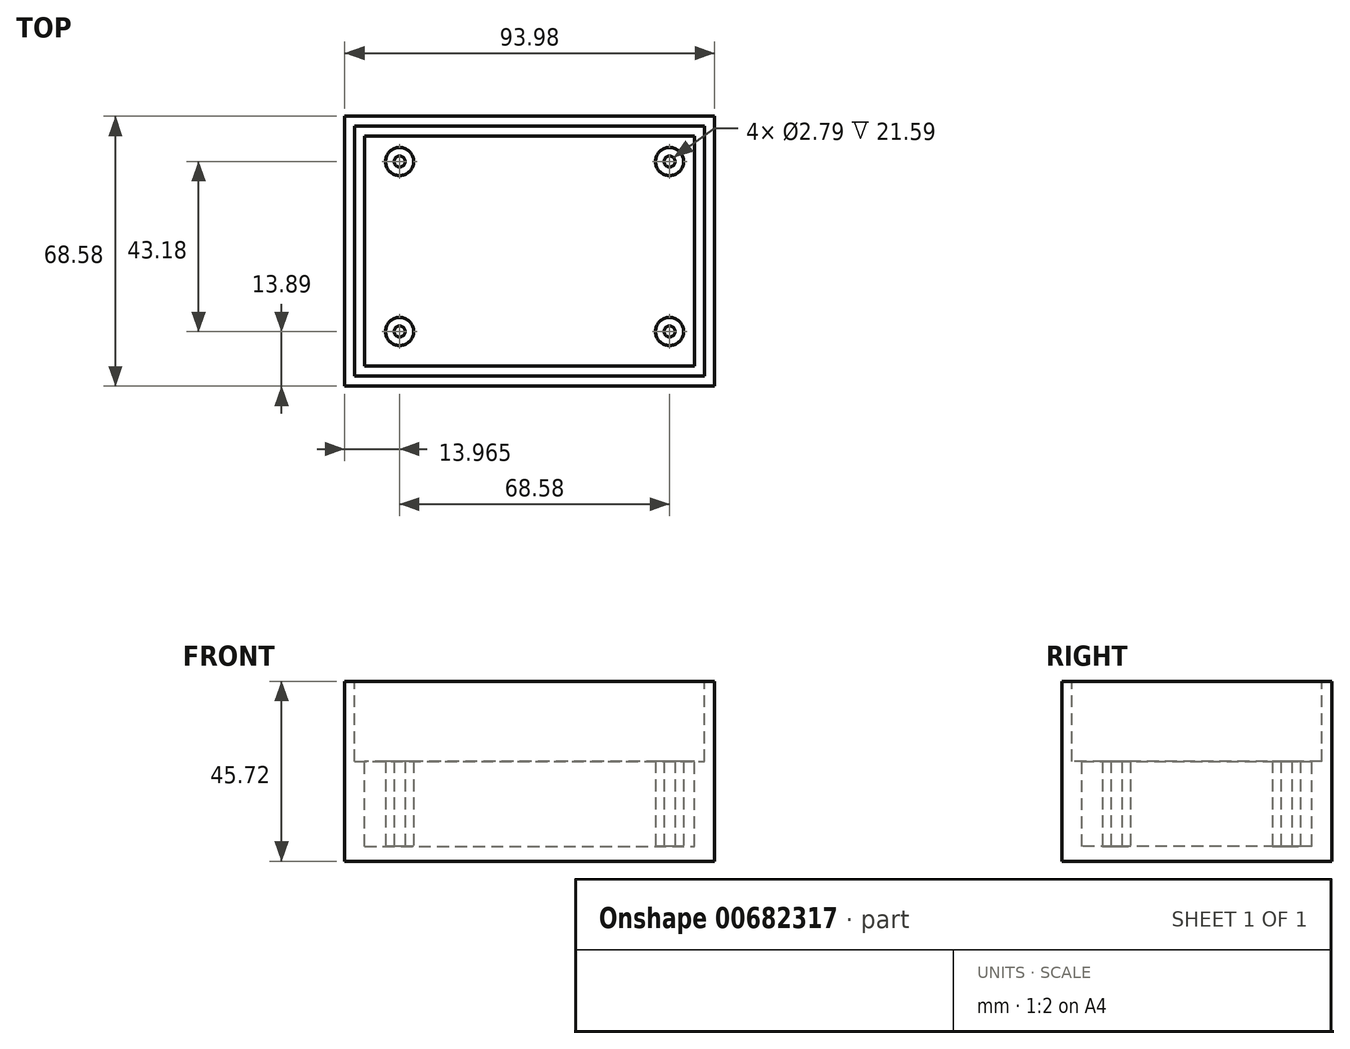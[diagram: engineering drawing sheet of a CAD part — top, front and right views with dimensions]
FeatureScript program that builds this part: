
annotation { "Feature Type Name" : "Feature", "Feature Type Description" : "" }
export const myFeature = defineFeature(function(context is Context, id is Id, definition is map)
    precondition{}
    {
        {
            var Q0;
            Q0=qCreatedBy(makeId("Top.planeOp"),FACE);
            var sketch = newSketch(context, id + "F0", { "sketchPlane" : qUnion([Q0])});
            skLineSegment(sketch, "E0.bottom", {"start": v(-123.06, 54.69) * mm, "end": v(-29.08, 54.69) * mm});
            skLineSegment(sketch, "E0.top", {"start": v(-123.06, -13.9) * mm, "end": v(-29.08, -13.9) * mm});
            skLineSegment(sketch, "E0.left", {"start": v(-123.06, 54.69) * mm, "end": v(-123.06, -13.9) * mm});
            skLineSegment(sketch, "E0.right", {"start": v(-29.08, 54.69) * mm, "end": v(-29.08, -13.9) * mm});
            skSolve(sketch);
        }
        {
            var Q0;
            Q0=makeQuery(id+"F0.imprint","IMPRINT",FACE,{"disambiguationData":[TD([[makeQuery(id+"F0.imprint","IMPRINT",EDGE,{"derivedFrom":sQuery(id+"F0.wireOp",EDGE,"E0.bottom")}),-1.0]])]});
            extrude(context, id + "F1", {"entities" : qUnion([Q0]), "depth" : 45.72 * mm, "offsetDistance" : 25.4 * mm});
        }
        {
            var Q0;
            Q0=makeQuery(id+"F1.opExtrude","CAP_FACE",FACE,{"disambiguationData":[OSD([sQuery(id+"F0.wireOp",EDGE,"E0.bottom"),sQuery(id+"F0.wireOp",EDGE,"E0.top"),sQuery(id+"F0.wireOp",EDGE,"E0.left"),sQuery(id+"F0.wireOp",EDGE,"E0.right")])],"isStart":false});
            var sketch = newSketch(context, id + "F2", { "sketchPlane" : qUnion([Q0])});
            skLineSegment(sketch, "E1.bottom", {"start": v(-117.98, 49.6) * mm, "end": v(-34.16, 49.6) * mm});
            skLineSegment(sketch, "E1.top", {"start": v(-117.98, -8.81) * mm, "end": v(-34.16, -8.81) * mm});
            skLineSegment(sketch, "E1.left", {"start": v(-117.98, 49.6) * mm, "end": v(-117.98, -8.81) * mm});
            skLineSegment(sketch, "E1.right", {"start": v(-34.16, 49.6) * mm, "end": v(-34.16, -8.81) * mm});
            skSolve(sketch);
        }
        {
            var Q0;
            Q0 = qSketchRegion(id + "F2", true);
            extrude(context, id + "F3", {"entities" : qUnion([Q0]), "operationType" : NewBodyOperationType.REMOVE, "oppositeDirection" : true, "depth" : 41.9 * mm, "offsetDistance" : 25.4 * mm});
        }
        {
            var Q0;
            Q0=makeQuery(id+"F3.boolean.opBoolean","COPY",FACE,{"derivedFrom":makeQuery(id+"F3.opExtrude","CAP_FACE",FACE,{"disambiguationData":[OSD([sQuery(id+"F2.wireOp",EDGE,"E1.bottom"),sQuery(id+"F2.wireOp",EDGE,"E1.top"),sQuery(id+"F2.wireOp",EDGE,"E1.left"),sQuery(id+"F2.wireOp",EDGE,"E1.right")])],"isStart":false})});
            var sketch = newSketch(context, id + "F4", { "sketchPlane" : qUnion([Q0])});
            skCircle(sketch, "E2", {"center": v(-109.1, 43.18) * mm, "radius": 3.56 * mm});
            skCircle(sketch, "E3", {"center": v(-40.51, 43.18) * mm, "radius": 3.56 * mm});
            skCircle(sketch, "E4", {"center": v(-109.1, 0) * mm, "radius": 3.56 * mm});
            skCircle(sketch, "E5", {"center": v(-40.51, 0) * mm, "radius": 3.56 * mm});
            skCircle(sketch, "E6", {"center": v(-40.51, 43.18) * mm, "radius": 1.4 * mm});
            skCircle(sketch, "E7", {"center": v(-109.1, 0) * mm, "radius": 1.4 * mm});
            skCircle(sketch, "E8", {"center": v(-40.51, 0) * mm, "radius": 1.4 * mm});
            skCircle(sketch, "E9", {"center": v(-109.1, 43.18) * mm, "radius": 1.4 * mm});
            skSolve(sketch);
        }
        {
            var Q0;
            Q0 = qSketchRegion(id + "F4", true);
            extrude(context, id + "F5", {"entities" : qUnion([Q0]), "operationType" : NewBodyOperationType.ADD, "depth" : 21.59 * mm, "offsetDistance" : 25.4 * mm});
        }
        {
            var Q0;
            Q0=makeQuery(id+"F1.opExtrude","CAP_FACE",FACE,{"disambiguationData":[OSD([sQuery(id+"F0.wireOp",EDGE,"E0.bottom"),sQuery(id+"F0.wireOp",EDGE,"E0.top"),sQuery(id+"F0.wireOp",EDGE,"E0.left"),sQuery(id+"F0.wireOp",EDGE,"E0.right")])],"isStart":false});
            var sketch = newSketch(context, id + "F6", { "sketchPlane" : qUnion([Q0])});
            skLineSegment(sketch, "E10.bottom", {"start": v(-120.52, 52.15) * mm, "end": v(-31.62, 52.15) * mm});
            skLineSegment(sketch, "E10.top", {"start": v(-120.52, -11.35) * mm, "end": v(-31.62, -11.35) * mm});
            skLineSegment(sketch, "E10.left", {"start": v(-120.52, 52.15) * mm, "end": v(-120.52, -11.35) * mm});
            skLineSegment(sketch, "E10.right", {"start": v(-31.62, 52.15) * mm, "end": v(-31.62, -11.35) * mm});
            skSolve(sketch);
        }
        {
            var Q0;
            Q0 = qSketchRegion(id + "F6", true);
            extrude(context, id + "F7", {"entities" : qUnion([Q0]), "operationType" : NewBodyOperationType.REMOVE, "oppositeDirection" : true, "depth" : 20.32 * mm, "offsetDistance" : 25.4 * mm});
        }
    });
